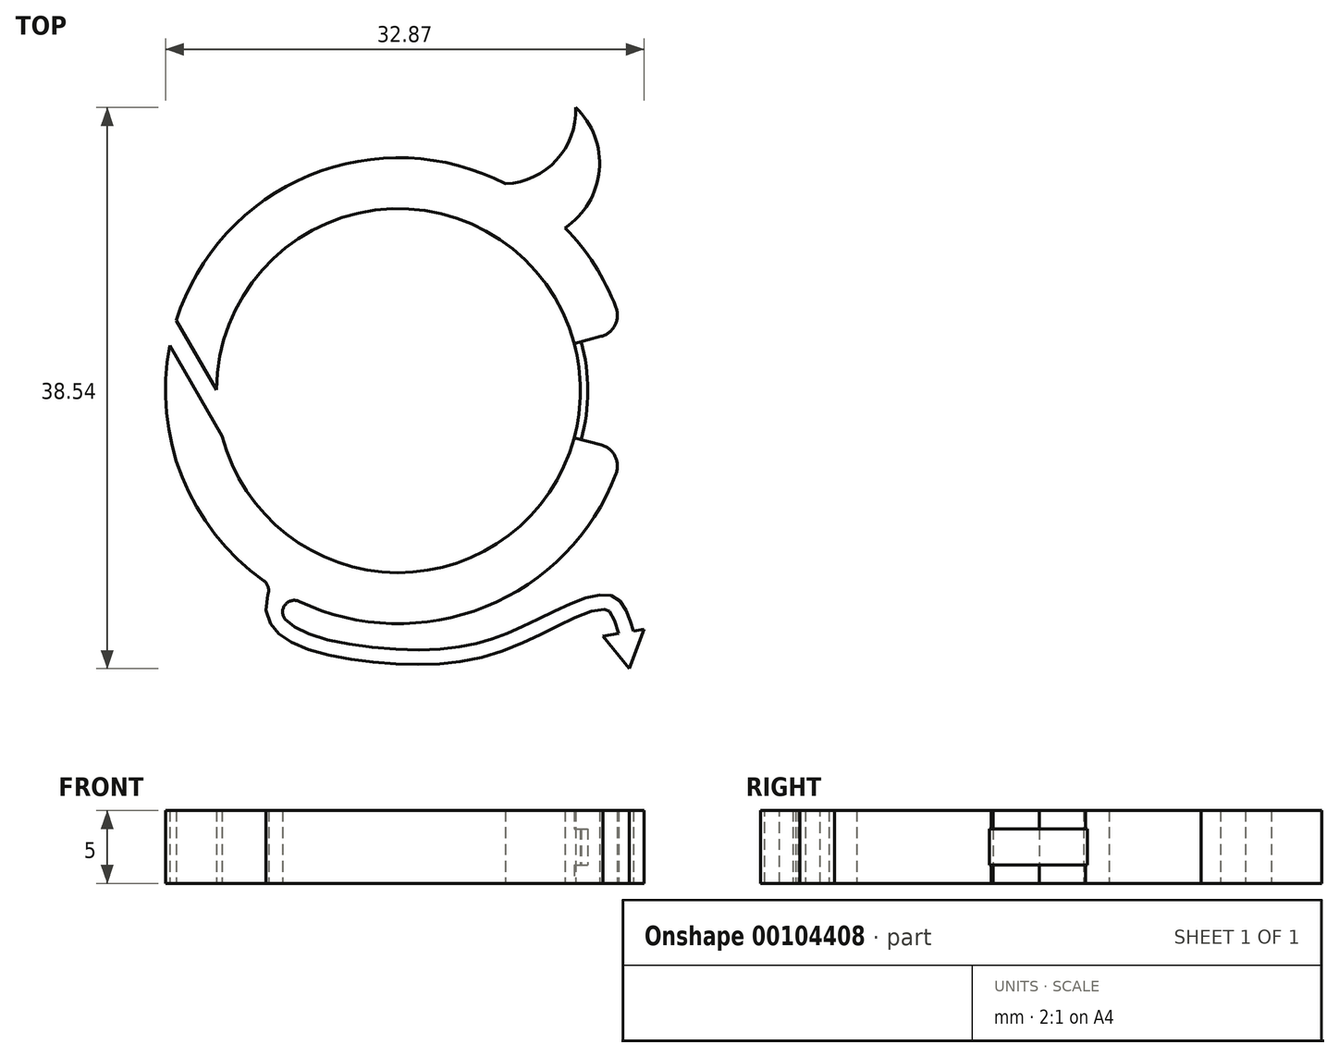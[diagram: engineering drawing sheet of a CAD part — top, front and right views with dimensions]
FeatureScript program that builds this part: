
annotation { "Feature Type Name" : "Feature", "Feature Type Description" : "" }
export const myFeature = defineFeature(function(context is Context, id is Id, definition is map)
    precondition{}
    {
        {
            var Q0;
            Q0=qCreatedBy(makeId("Top.planeOp"),FACE);
            var sketch = newSketch(context, id + "F0", { "sketchPlane" : qUnion([Q0])});
            skCircle(sketch, "E0", {"center": v(0, 0) * mm, "radius": 12.5 * mm});
            skLineSegment(sketch, "E1", {"start": v(12.07, 3.24) * mm, "end": v(15.45, 4.14) * mm});
            skLineSegment(sketch, "E2.MirrorCS", {"start": v(12.07, -3.24) * mm, "end": v(15.45, -4.14) * mm});
            skPoint(sketch, "E3", {"position": v(12.07, 3.24) * mm});
            skPoint(sketch, "E4", {"position": v(12.07, -3.24) * mm});
            skArc(sketch, "E5", {"start": v(12.56, -3.36) * mm, "mid": v(13, 0) * mm, "end": v(12.56, 3.36) * mm});
            skLineSegment(sketch, "E6", {"start": v(12.56, 3.36) * mm, "end": v(12.73, 2.63) * mm, "construction": true});
            skLineSegment(sketch, "E7", {"start": v(-16, 0) * mm, "end": v(-12.5, 0) * mm, "construction": true});
            skArc(sketch, "E8", {"start": v(7.36, 14.2) * mm, "mid": v(10.85, 15.83) * mm, "end": v(12.18, 19.45) * mm});
            skArc(sketch, "E9", {"start": v(11.44, 11.18) * mm, "mid": v(13.8, 15.14) * mm, "end": v(12.18, 19.45) * mm});
            skArc(sketch, "E10.MirrorCS", {"start": v(-7.36, 14.2) * mm, "mid": v(-10.85, 15.83) * mm, "end": v(-12.18, 19.45) * mm});
            skArc(sketch, "E11.MirrorCS", {"start": v(-11.44, 11.18) * mm, "mid": v(-13.8, 15.14) * mm, "end": v(-12.18, 19.45) * mm});
            skPoint(sketch, "E12", {"position": v(-12.18, 19.45) * mm});
            skPoint(sketch, "E13", {"position": v(-7.36, 14.2) * mm});
            skPoint(sketch, "E14", {"position": v(-11.44, 11.18) * mm});
            skPoint(sketch, "E15", {"position": v(12.18, 19.45) * mm});
            skPoint(sketch, "E16", {"position": v(7.36, 14.2) * mm});
            skPoint(sketch, "E17", {"position": v(11.44, 11.18) * mm});
            skPoint(sketch, "E18", {"position": v(13.8, 15.14) * mm});
            skPoint(sketch, "E19", {"position": v(10.85, 15.83) * mm});
            skPoint(sketch, "E20", {"position": v(-10.85, 15.83) * mm});
            skPoint(sketch, "E21", {"position": v(-13.8, 15.14) * mm});
            skCircle(sketch, "E22", {"center": v(0, 0) * mm, "radius": 16 * mm});
            skLineSegment(sketch, "E23", {"start": v(-12.1, -3.1) * mm, "end": v(-15.7, 3.1) * mm});
            skLineSegment(sketch, "E24", {"start": v(-12.1, -3.1) * mm, "end": v(-12.1, 3.1) * mm, "construction": true});
            skLineSegment(sketch, "E25", {"start": v(-15.7, 3.1) * mm, "end": v(-15.7, -3.1) * mm, "construction": true});
            skLineSegment(sketch, "E26", {"start": v(-12.1, -0.6) * mm, "end": v(-15.25, 4.84) * mm});
            skFitSpline(sketch, "E27", {"points": [v(-7.81, -13.96) * mm, v(-7.62, -15.88) * mm, v(2.28, -17.78) * mm, v(9.38, -15.8) * mm, v(14.77, -14.14) * mm, v(16.14, -16.51) * mm], "startDerivative": vector(-8.6, -14.32) * mm, "endDerivative": vector(5.66, -16.46) * mm});
            skFitSpline(sketch, "E28.0", {"points": [v(-8.67, -13.45) * mm, v(-8.8, -13.67) * mm, v(-9.02, -14.14) * mm, v(-9.11, -14.84) * mm, v(-9.02, -15.44) * mm, v(-8.86, -15.88) * mm, v(-8.6, -16.3) * mm, v(-8.27, -16.66) * mm, v(-7.88, -16.96) * mm, v(-7.31, -17.31) * mm, v(-6.5, -17.67) * mm, v(-5.4, -18.02) * mm, v(-4.17, -18.3) * mm, v(-2.86, -18.52) * mm, v(-1.5, -18.68) * mm, v(-0.14, -18.78) * mm, v(1.19, -18.81) * mm, v(2.45, -18.78) * mm, v(3.61, -18.7) * mm, v(4.68, -18.53) * mm, v(6.02, -18.25) * mm, v(7.24, -17.85) * mm, v(8.42, -17.36) * mm, v(9.29, -16.96) * mm, v(10.18, -16.53) * mm, v(11.08, -16.08) * mm, v(11.96, -15.66) * mm, v(12.78, -15.32) * mm, v(13.5, -15.08) * mm, v(13.97, -15) * mm, v(14.22, -15.01) * mm, v(14.32, -15.03) * mm, v(14.36, -15.05) * mm, v(14.38, -15.06) * mm, v(14.43, -15.1) * mm, v(14.51, -15.18) * mm, v(14.65, -15.36) * mm, v(14.82, -15.72) * mm, v(15.01, -16.26) * mm, v(15.13, -16.64) * mm, v(15.2, -16.84) * mm]});
            skFitSpline(sketch, "E29", {"points": [v(12.74, -15.35) * mm, v(14.05, -15.08) * mm, v(14.72, -15.74) * mm, v(14.84, -16.72) * mm], "startDerivative": vector(2.92, 0.98) * mm, "endDerivative": vector(0.86, -2.3) * mm});
            skLineSegment(sketch, "E30", {"start": v(14.03, -16.85) * mm, "end": v(16.87, -16.4) * mm});
            skLineSegment(sketch, "E31", {"start": v(14.03, -16.85) * mm, "end": v(15.85, -19.09) * mm});
            skLineSegment(sketch, "E32", {"start": v(15.85, -19.09) * mm, "end": v(16.87, -16.4) * mm});
            skSolve(sketch);
        }
        {
            var Q0;
            {var subQ1=sQuery(id+"F0.wireOp",EDGE,"E1");var subQ6=sQuery(id+"F0.wireOp",EDGE,"E0");var subQ7=makeQuery(id+"F0.imprint","INTERSECT",VERTEX,{"derivedFrom":[subQ6,subQ1]});Q0=makeQuery(id+"F0.imprint","IMPRINT",FACE,{"disambiguationData":[TD([[makeQuery(id+"F0.imprint","IMPRINT",EDGE,{"disambiguationData":[TD([[subQ7,-1.0]])],"derivedFrom":subQ6}),-1.0]])]});}
            var Q1;
            {var subQ3=sQuery(id+"F0.wireOp",EDGE,"E23");Q1=makeQuery(id+"F0.imprint","IMPRINT",FACE,{"disambiguationData":[TD([[makeQuery(id+"F0.imprint","IMPRINT",EDGE,{"derivedFrom":subQ3}),1.0]])]});}
            var Q2;
            {var subQ2=sQuery(id+"F0.wireOp",EDGE,"E27");Q2=makeQuery(id+"F0.imprint","IMPRINT",FACE,{"disambiguationData":[TD([[makeQuery(id+"F0.imprint","IMPRINT",EDGE,{"derivedFrom":subQ2}),-1.0]])]});}
            var Q3;
            {var subQ0=sQuery(id+"F0.wireOp",EDGE,"E31");Q3=makeQuery(id+"F0.imprint","IMPRINT",FACE,{"disambiguationData":[TD([[makeQuery(id+"F0.imprint","IMPRINT",EDGE,{"derivedFrom":subQ0}),1.0]])]});}
            var Q4;
            {var subQ0=sQuery(id+"F0.wireOp",EDGE,"E11.MirrorCS");var subQ1=sQuery(id+"F0.wireOp",EDGE,"E10.MirrorCS");var subQ2=makeQuery(id+"F0.imprint","INTERSECT",VERTEX,{"derivedFrom":[subQ1,subQ0]});Q4=makeQuery(id+"F0.imprint","IMPRINT",FACE,{"disambiguationData":[TD([[makeQuery(id+"F0.imprint","IMPRINT",EDGE,{"disambiguationData":[TD([[subQ2,1.0]])],"derivedFrom":subQ1}),1.0]])]});}
            var Q5;
            {var subQ0=sQuery(id+"F0.wireOp",EDGE,"E9");var subQ1=sQuery(id+"F0.wireOp",EDGE,"E8");var subQ2=makeQuery(id+"F0.imprint","INTERSECT",VERTEX,{"derivedFrom":[subQ1,subQ0]});Q5=makeQuery(id+"F0.imprint","IMPRINT",FACE,{"disambiguationData":[TD([[makeQuery(id+"F0.imprint","IMPRINT",EDGE,{"disambiguationData":[TD([[subQ2,1.0]])],"derivedFrom":subQ1}),-1.0]])]});}
            extrude(context, id + "F1", {"entities" : qUnion([Q0, Q1, Q2, Q3, Q4, Q5]), "endBound" : BoundingType.SYMMETRIC, "depth" : 5 * mm});
        }
        {
            var Q0;
            {var subQ5=sQuery(id+"F0.wireOp",EDGE,"E5");Q0=makeQuery(id+"F0.imprint","IMPRINT",FACE,{"disambiguationData":[TD([[makeQuery(id+"F0.imprint","IMPRINT",EDGE,{"derivedFrom":subQ5}),1.0]])]});}
            extrude(context, id + "F2", {"entities" : qUnion([Q0]), "operationType" : NewBodyOperationType.ADD, "endBound" : BoundingType.SYMMETRIC, "depth" : 2.5 * mm});
        }
        {
            var Q0;
            Q0=makeQuery(id+"F1.opExtrude","SWEPT_EDGE",EDGE,{"disambiguationData":[OSD([sQuery(id+"F0.wireOp",EDGE,"E2.MirrorCS"),sQuery(id+"F0.wireOp",EDGE,"E22")])]});
            var Q1;
            Q1=makeQuery(id+"F1.opExtrude","SWEPT_EDGE",EDGE,{"disambiguationData":[OSD([sQuery(id+"F0.wireOp",EDGE,"E2.MirrorCS"),sQuery(id+"F0.wireOp",EDGE,"E22")])]});
            var Q2;
            Q2=makeQuery(id+"F1.opExtrude","SWEPT_EDGE",EDGE,{"disambiguationData":[OSD([sQuery(id+"F0.wireOp",EDGE,"E1"),sQuery(id+"F0.wireOp",EDGE,"E22")])]});
            var Q3;
            Q3=makeQuery(id+"F1.opExtrude","SWEPT_EDGE",EDGE,{"disambiguationData":[OSD([sQuery(id+"F0.wireOp",EDGE,"E1"),sQuery(id+"F0.wireOp",EDGE,"E22")])]});
            var Q4;
            Q4=makeQuery(id+"F1.opExtrude","SWEPT_EDGE",EDGE,{"disambiguationData":[OSD([sQuery(id+"F0.wireOp",EDGE,"E2.MirrorCS"),sQuery(id+"F0.wireOp",EDGE,"E22")])]});
            fillet(context, id + "F3", {"entities" : qUnion([Q0, Q1, Q2, Q3, Q4]), "radius" : 1.5 * mm, "tangentPropagation" : true, "allowEdgeOverflow" : false});
        }
        {
            var Q0;
            {var subQ0=sQuery(id+"F0.wireOp",EDGE,"E0");var subQ1=makeQuery(id+"F0.imprint","INTERSECT",VERTEX,{"derivedFrom":[subQ0,sQuery(id+"F0.wireOp",EDGE,"E1")]});Q0=makeQuery(id+"F0.imprint","IMPRINT",FACE,{"disambiguationData":[TD([[makeQuery(id+"F0.imprint","IMPRINT",EDGE,{"disambiguationData":[TD([[subQ1,-1.0]])],"derivedFrom":subQ0}),1.0]])]});}
            extrude(context, id + "F4", {"entities" : qUnion([Q0]), "operationType" : NewBodyOperationType.REMOVE, "endBound" : BoundingType.SYMMETRIC, "oppositeDirection" : true, "depth" : 5 * mm});
        }
        {
            var Q0;
            Q0=makeQuery(id+"F1.opExtrude","SWEPT_EDGE",EDGE,{"disambiguationData":[OSD([sQuery(id+"F0.wireOp",EDGE,"E22"),sQuery(id+"F0.wireOp",EDGE,"E27")])]});
            var Q1;
            Q1=makeQuery(id+"F1.opExtrude","SWEPT_EDGE",EDGE,{"disambiguationData":[OSD([sQuery(id+"F0.wireOp",EDGE,"E22"),sQuery(id+"F0.wireOp",EDGE,"E28.0")])]});
            fillet(context, id + "F5", {"entities" : qUnion([Q0, Q1]), "radius" : 0.8 * mm, "tangentPropagation" : true, "allowEdgeOverflow" : false});
        }
    });
